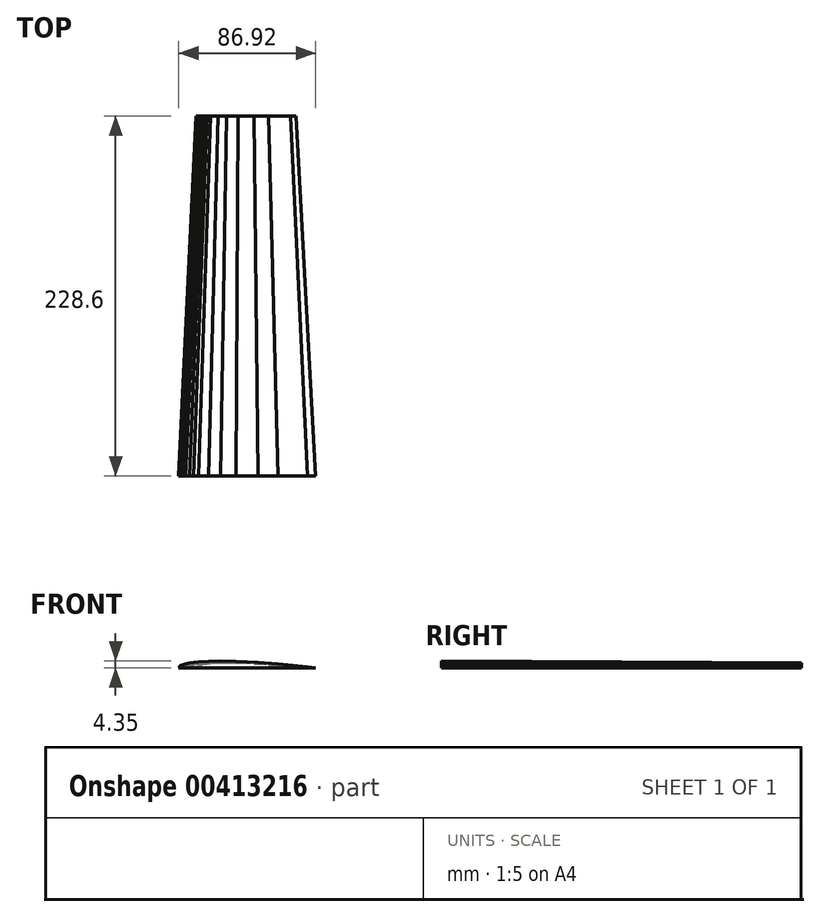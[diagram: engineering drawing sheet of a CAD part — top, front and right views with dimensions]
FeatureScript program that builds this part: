
annotation { "Feature Type Name" : "Feature", "Feature Type Description" : "" }
export const myFeature = defineFeature(function(context is Context, id is Id, definition is map)
    precondition{}
    {
        {
            var Q0;
            Q0=qCreatedBy(makeId("Front.planeOp"),FACE);
            cPlane(context, id + "F0", {"entities" : qUnion([Q0]), "cplaneType" : CPlaneType.OFFSET, "offset" : 228.6 * mm, "oppositeDirection" : true, "width" : 152.4 * mm, "height" : 152.4 * mm});
        }
        {
            var Q0;
            Q0=qCreatedBy(makeId("Front.planeOp"),FACE);
            var sketch = newSketch(context, id + "F1", { "sketchPlane" : qUnion([Q0])});
            skLineSegment(sketch, "E0", {"start": v(-38.13, 0) * mm, "end": v(-125.05, 0) * mm});
            skPoint(sketch, "E1.MirrorP", {"position": v(-125.05, 0) * mm});
            skLineSegment(sketch, "E2.MirrorCS", {"start": v(-118.12, 3.13) * mm, "end": v(-115.6, 3.48) * mm});
            skLineSegment(sketch, "E3.MirrorCS", {"start": v(-43.17, 0.7) * mm, "end": v(-38.13, 0) * mm});
            skLineSegment(sketch, "E4.MirrorCS", {"start": v(-120.64, 2.6) * mm, "end": v(-118.12, 3.13) * mm});
            skLineSegment(sketch, "E5.MirrorCS", {"start": v(-122.54, 2) * mm, "end": v(-120.64, 2.6) * mm});
            skLineSegment(sketch, "E6.MirrorCS", {"start": v(-122.54, 2) * mm, "end": v(-123.8, 1.48) * mm});
            skLineSegment(sketch, "E7.MirrorCS", {"start": v(-125.05, 0) * mm, "end": v(-123.8, 1.48) * mm});
            skPoint(sketch, "E8.MirrorP", {"position": v(-40.65, 0.35) * mm});
            skLineSegment(sketch, "E9.MirrorCS", {"start": v(-55.76, 1.91) * mm, "end": v(-43.17, 0.7) * mm});
            skLineSegment(sketch, "E10.MirrorCS", {"start": v(-115.6, 3.48) * mm, "end": v(-112.45, 3.82) * mm});
            skLineSegment(sketch, "E11.MirrorCS", {"start": v(-112.45, 3.82) * mm, "end": v(-106.16, 4.17) * mm});
            skLineSegment(sketch, "E12.MirrorCS", {"start": v(-106.16, 4.17) * mm, "end": v(-98.6, 4.35) * mm});
            skLineSegment(sketch, "E13.MirrorCS", {"start": v(-98.6, 4.35) * mm, "end": v(-88.52, 4.17) * mm});
            skLineSegment(sketch, "E14.MirrorCS", {"start": v(-88.52, 4.17) * mm, "end": v(-74.66, 3.39) * mm});
            skLineSegment(sketch, "E15.MirrorCS", {"start": v(-74.66, 3.39) * mm, "end": v(-62.07, 2.48) * mm});
            skLineSegment(sketch, "E16.MirrorCS", {"start": v(-62.07, 2.48) * mm, "end": v(-55.76, 1.91) * mm});
            skSolve(sketch);
        }
        {
            var Q0;
            Q0=qCreatedBy(id+"F0.planeOp",FACE);
            var sketch = newSketch(context, id + "F2", { "sketchPlane" : qUnion([Q0])});
            skPoint(sketch, "E17", {"position": v(-113.92, 0) * mm});
            skLineSegment(sketch, "E18.MirrorCS", {"start": v(-113.92, 0.07) * mm, "end": v(-113, 1.15) * mm});
            skLineSegment(sketch, "E19.MirrorCS", {"start": v(-112.09, 1.53) * mm, "end": v(-113, 1.15) * mm});
            skLineSegment(sketch, "E20.MirrorCS", {"start": v(-112.09, 1.53) * mm, "end": v(-110.7, 1.98) * mm});
            skLineSegment(sketch, "E21.MirrorCS", {"start": v(-110.7, 1.98) * mm, "end": v(-108.86, 2.36) * mm});
            skLineSegment(sketch, "E22.MirrorCS", {"start": v(-108.86, 2.36) * mm, "end": v(-107.03, 2.61) * mm});
            skPoint(sketch, "E23.MirrorP", {"position": v(-113.92, 0.07) * mm});
            skLineSegment(sketch, "E24.MirrorCS", {"start": v(-107.03, 2.61) * mm, "end": v(-104.72, 2.87) * mm});
            skLineSegment(sketch, "E25.MirrorCS", {"start": v(-94.6, 3.25) * mm, "end": v(-87.23, 3.12) * mm});
            skPoint(sketch, "E26.MirrorP", {"position": v(-108.86, 2.36) * mm});
            skLineSegment(sketch, "E27.MirrorCS", {"start": v(-77.11, 2.55) * mm, "end": v(-67.9, 1.88) * mm});
            skPoint(sketch, "E28.MirrorP", {"position": v(-112.09, 1.53) * mm});
            skPoint(sketch, "E29.MirrorP", {"position": v(-54.1, 0.58) * mm});
            skPoint(sketch, "E30.MirrorP", {"position": v(-67.9, 1.88) * mm});
            skPoint(sketch, "E31.MirrorP", {"position": v(-87.23, 3.12) * mm});
            skPoint(sketch, "E32.MirrorP", {"position": v(-100.12, 3.12) * mm});
            skPoint(sketch, "E33.MirrorP", {"position": v(-107.03, 2.61) * mm});
            skPoint(sketch, "E34.MirrorP", {"position": v(-110.7, 1.98) * mm});
            skPoint(sketch, "E35.MirrorP", {"position": v(-113, 1.15) * mm});
            skLineSegment(sketch, "E36.MirrorCS", {"start": v(-63.3, 1.47) * mm, "end": v(-54.1, 0.58) * mm});
            skLineSegment(sketch, "E37.MirrorCS", {"start": v(-54.1, 0.58) * mm, "end": v(-50.42, 0.07) * mm});
            skLineSegment(sketch, "E38.MirrorCS", {"start": v(-50.42, 0.07) * mm, "end": v(-113.92, 0.07) * mm});
            skPoint(sketch, "E39.MirrorP", {"position": v(-63.3, 1.47) * mm});
            skPoint(sketch, "E40.MirrorP", {"position": v(-77.11, 2.55) * mm});
            skPoint(sketch, "E41.MirrorP", {"position": v(-94.6, 3.25) * mm});
            skLineSegment(sketch, "E42.MirrorCS", {"start": v(-104.72, 2.87) * mm, "end": v(-100.12, 3.12) * mm});
            skPoint(sketch, "E43.MirrorP", {"position": v(-104.72, 2.87) * mm});
            skLineSegment(sketch, "E44.MirrorCS", {"start": v(-100.12, 3.12) * mm, "end": v(-94.6, 3.25) * mm});
            skLineSegment(sketch, "E45.MirrorCS", {"start": v(-67.9, 1.88) * mm, "end": v(-63.3, 1.47) * mm});
            skLineSegment(sketch, "E46.MirrorCS", {"start": v(-87.23, 3.12) * mm, "end": v(-77.11, 2.55) * mm});
            skSolve(sketch);
        }
        {
            var Q0;
            Q0 = qSketchRegion(id + "F1", true);
            var Q1;
            Q1 = qSketchRegion(id + "F2", true);
            loft(context, id + "F3", {"sheetProfilesArray" : [{ "sheetProfileEntities" : qUnion([Q0]) }, { "sheetProfileEntities" : qUnion([Q1]) }]});
        }
    });
